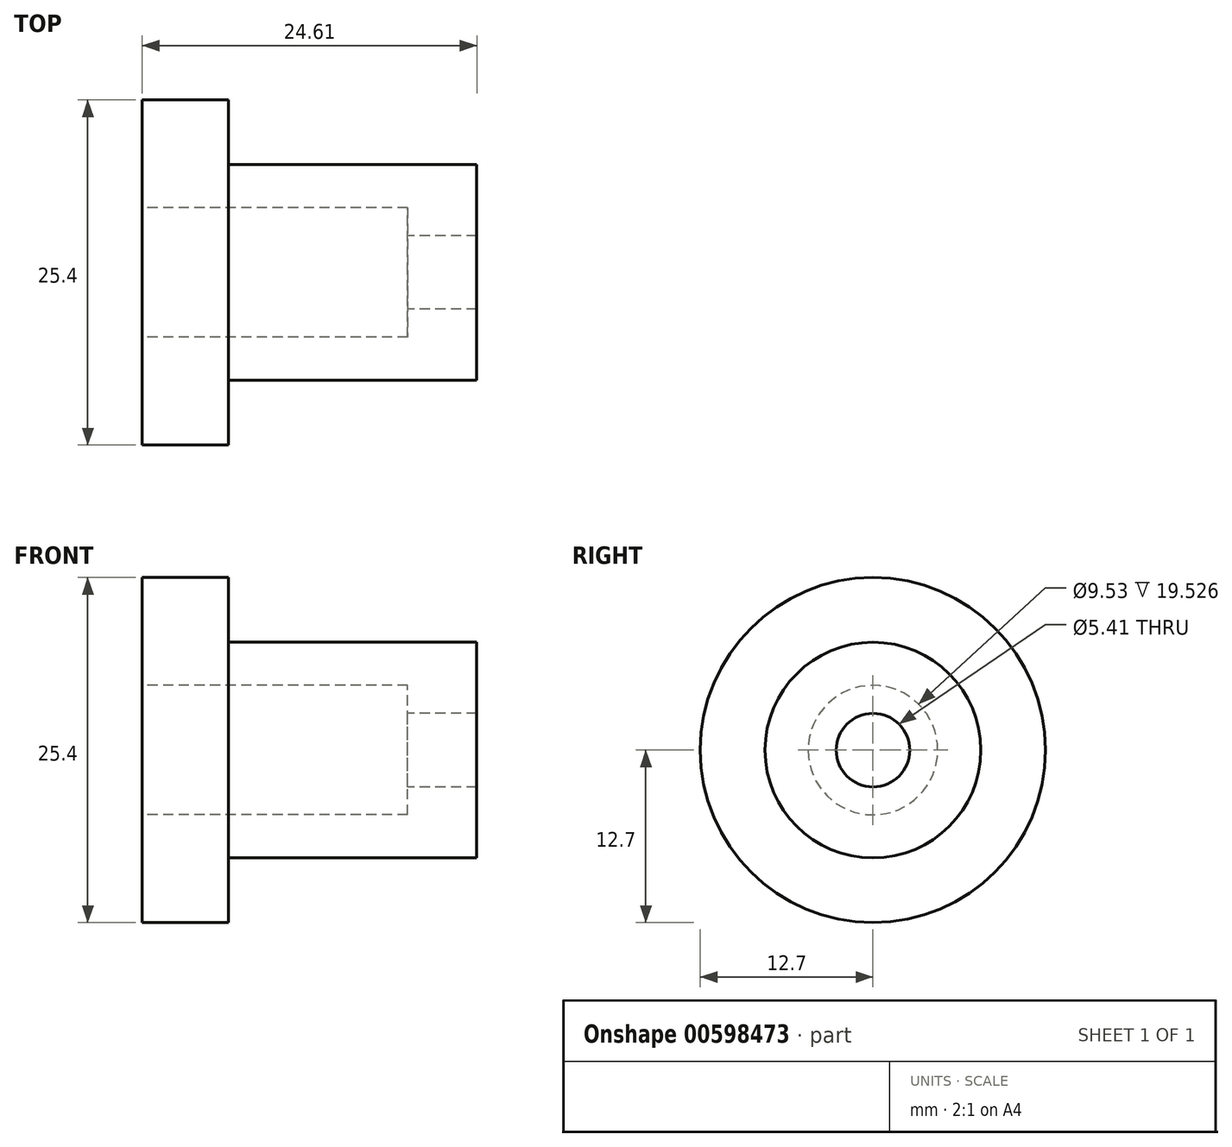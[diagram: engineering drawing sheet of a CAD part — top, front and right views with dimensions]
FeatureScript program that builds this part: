
annotation { "Feature Type Name" : "Feature", "Feature Type Description" : "" }
export const myFeature = defineFeature(function(context is Context, id is Id, definition is map)
    precondition{}
    {
        {
            var Q0;
            Q0=qCreatedBy(makeId("Right.planeOp"),FACE);
            var sketch = newSketch(context, id + "F0", { "sketchPlane" : qUnion([Q0])});
            skCircle(sketch, "E0", {"center": v(0, 0) * mm, "radius": 12.7 * mm});
            skCircle(sketch, "E1", {"center": v(0, 0) * mm, "radius": 7.94 * mm});
            skCircle(sketch, "E2", {"center": v(0, 0) * mm, "radius": 4.76 * mm});
            skSolve(sketch);
        }
        {
            var Q0;
            Q0=makeQuery(id+"F0.imprint","IMPRINT",FACE,{"disambiguationData":[TD([[makeQuery(id+"F0.imprint","IMPRINT",EDGE,{"derivedFrom":sQuery(id+"F0.wireOp",EDGE,"E0")}),1.0]])]});
            extrude(context, id + "F1", {"entities" : qUnion([Q0]), "depth" : 6.35 * mm, "offsetDistance" : 25.4 * mm});
        }
        {
            var Q0;
            Q0=makeQuery(id+"F0.imprint","IMPRINT",FACE,{"disambiguationData":[TD([[makeQuery(id+"F0.imprint","IMPRINT",EDGE,{"derivedFrom":sQuery(id+"F0.wireOp",EDGE,"E1")}),1.0]])]});
            extrude(context, id + "F2", {"entities" : qUnion([Q0]), "operationType" : NewBodyOperationType.ADD, "depth" : 24.6 * mm, "offsetDistance" : 25.4 * mm});
        }
        {
            var Q0;
            Q0=makeQuery(id+"F2.opExtrude","CAP_FACE",FACE,{"disambiguationData":[OSD([sQuery(id+"F0.wireOp",EDGE,"E1"),sQuery(id+"F0.wireOp",EDGE,"E2")])],"isStart":false});
            var sketch = newSketch(context, id + "F3", { "sketchPlane" : qUnion([Q0])});
            skCircle(sketch, "E3", {"center": v(0, 0) * mm, "radius": 3.18 * mm});
            skSolve(sketch);
        }
        {
            var Q0;
            Q0=makeQuery(id+"F3.imprint","IMPRINT",FACE,{"disambiguationData":[TD([[makeQuery(id+"F3.imprint","IMPRINT",EDGE,{"derivedFrom":makeQuery(id+"F2.opExtrude","CAP_EDGE",EDGE,{"disambiguationData":[OSD([sQuery(id+"F0.wireOp",EDGE,"E2")])],"isStart":false})}),1.0]])]});
            extrude(context, id + "F4", {"entities" : qUnion([Q0]), "operationType" : NewBodyOperationType.ADD, "oppositeDirection" : true, "depth" : 5.08 * mm, "offsetDistance" : 25.4 * mm});
        }
        {
            var Q0;
            Q0=makeQuery(id+"F3.imprint","IMPRINT",FACE,{"disambiguationData":[TD([[makeQuery(id+"F3.imprint","IMPRINT",EDGE,{"derivedFrom":sQuery(id+"F3.wireOp",EDGE,"E3")}),1.0]])]});
            extrude(context, id + "F5", {"entities" : qUnion([Q0]), "operationType" : NewBodyOperationType.ADD, "oppositeDirection" : true, "depth" : 5.08 * mm, "offsetDistance" : 25.4 * mm});
        }
        {
            var Q0;
            Q0=sQuery(id+"F3.wireOp",VERTEX,"E3.center");
            var Q1;
            Q1=makeQuery(id+"F1.opExtrude","SWEPT_BODY",BODY,{"disambiguationData":[OSD([sQuery(id+"F0.wireOp",EDGE,"E0"),sQuery(id+"F0.wireOp",EDGE,"E1")])]});
            hole(context, id + "F6", {"style" : HoleStyle.SIMPLE, "endStyle" : HoleEndStyle.THROUGH, "standardTappedOrClearance" : lookupTablePath({ "standard" : "ANSI", "engagement" : "75%", "pitch" : "28 tpi", "size" : "1/4", "type" : "Tapped" }), "standardBlindInLast" : lookupTablePath({ "standard" : "ANSI", "engagement" : "75%", "pitch" : "28 tpi", "size" : "1/4", "type" : "Tapped" }), "holeDiameter" : 5.4 * mm, "majorDiameter" : 6.35 * mm, "showTappedDepth" : true, "isTappedThrough" : true, "tappedDepth" : 22.7 * mm, "tapClearance" : 3, "locations" : qUnion([Q0]), "scope" : qUnion([Q1]), "startStyle" : HoleStartStyle.SKETCH});
        }
    });
